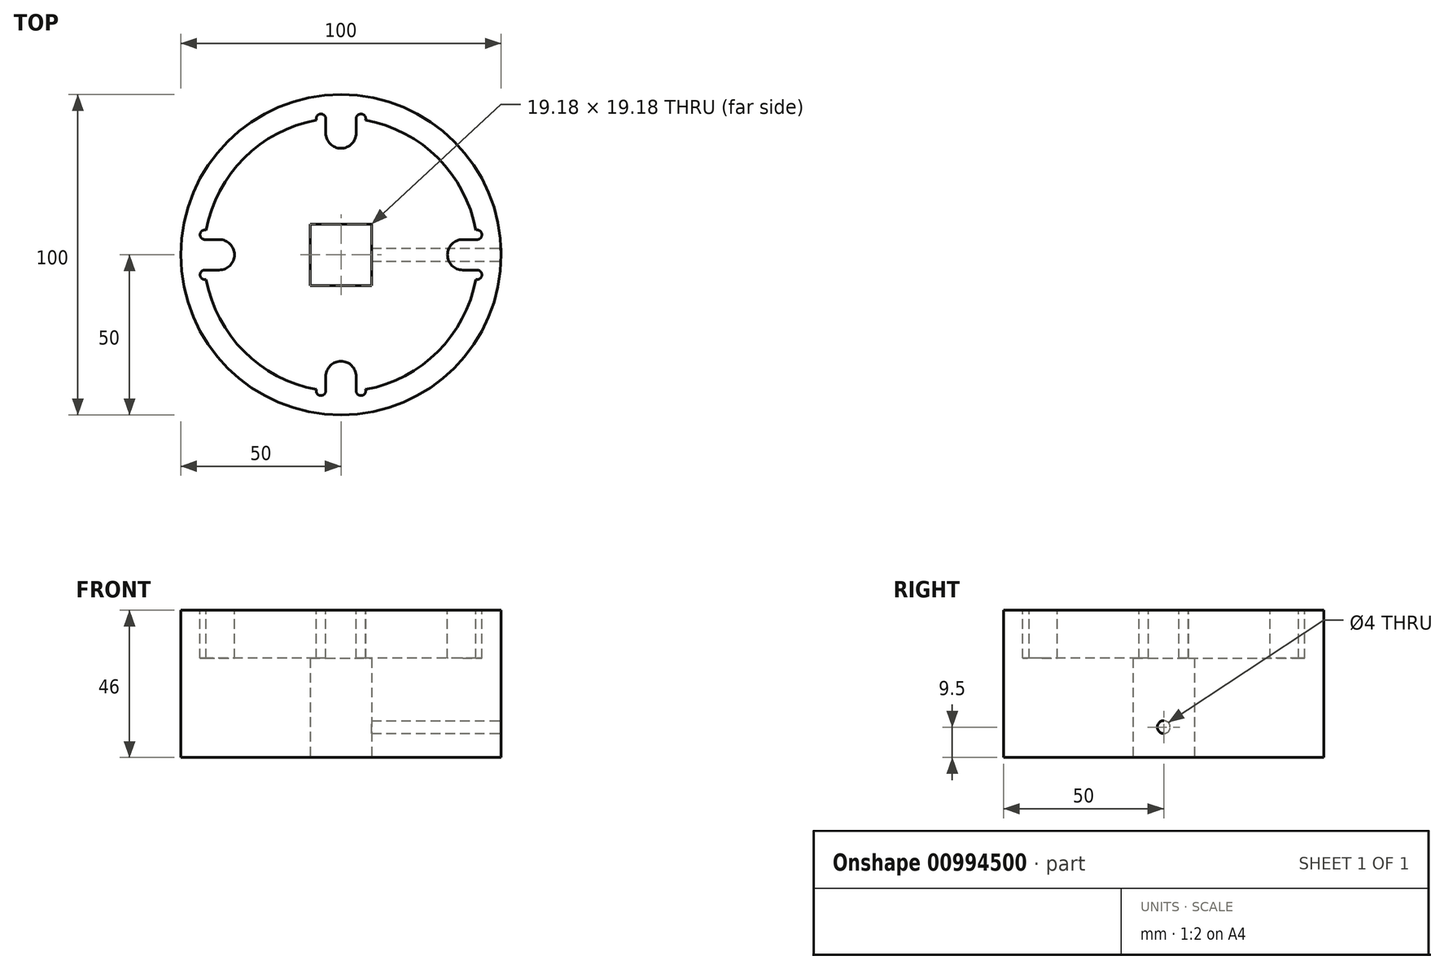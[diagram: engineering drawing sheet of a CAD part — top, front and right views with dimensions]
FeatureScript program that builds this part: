
annotation { "Feature Type Name" : "Feature", "Feature Type Description" : "" }
export const myFeature = defineFeature(function(context is Context, id is Id, definition is map)
    precondition{}
    {
        {
            var Q0;
            Q0=qCreatedBy(makeId("Top.planeOp"),FACE);
            var sketch = newSketch(context, id + "F0", { "sketchPlane" : qUnion([Q0])});
            skCircle(sketch, "E0", {"center": v(0, 0) * mm, "radius": 50 * mm});
            skSolve(sketch);
        }
        {
            var Q0;
            Q0 = qSketchRegion(id + "F0", true);
            extrude(context, id + "F1", {"entities" : qUnion([Q0]), "depth" : 46 * mm, "offsetDistance" : 25 * mm});
        }
        {
            var Q0;
            Q0=makeQuery(id+"F1.opExtrude","CAP_FACE",FACE,{"disambiguationData":[OSD([sQuery(id+"F0.wireOp",EDGE,"E0")])],"isStart":false});
            var sketch = newSketch(context, id + "F2", { "sketchPlane" : qUnion([Q0])});
            skArc(sketch, "E1", {"start": v(-7.69, 42.05) * mm, "mid": v(-30.23, 30.23) * mm, "end": v(-42.05, 7.69) * mm});
            skLineSegment(sketch, "E2.0", {"start": v(-42.49, -4.75) * mm, "end": v(-38, -4.75) * mm});
            skLineSegment(sketch, "E3.0", {"start": v(-42.49, 4.75) * mm, "end": v(-38, 4.75) * mm});
            skLineSegment(sketch, "E4.0", {"start": v(-4.75, 42.49) * mm, "end": v(-4.75, 38) * mm});
            skLineSegment(sketch, "E5.0", {"start": v(4.75, 42.49) * mm, "end": v(4.75, 38) * mm});
            skArc(sketch, "E6.trimOffspring", {"start": v(-42.05, -7.69) * mm, "mid": v(-30.23, -30.23) * mm, "end": v(-7.69, -42.05) * mm});
            skArc(sketch, "E7.trimOffspring", {"start": v(7.69, -42.05) * mm, "mid": v(30.23, -30.23) * mm, "end": v(42.05, -7.69) * mm});
            skLineSegment(sketch, "E8.trimOffspring", {"start": v(38, 4.75) * mm, "end": v(42.49, 4.75) * mm});
            skLineSegment(sketch, "E9.trimOffspring", {"start": v(38, -4.75) * mm, "end": v(42.49, -4.75) * mm});
            skLineSegment(sketch, "E10.trimOffspring", {"start": v(-4.75, -38) * mm, "end": v(-4.75, -42.49) * mm});
            skLineSegment(sketch, "E11.trimOffspring", {"start": v(4.75, -38) * mm, "end": v(4.75, -42.49) * mm});
            skArc(sketch, "E12.trimOffspring", {"start": v(42.05, 7.69) * mm, "mid": v(30.23, 30.23) * mm, "end": v(7.69, 42.05) * mm});
            skArc(sketch, "E13", {"start": v(-38, -4.75) * mm, "mid": v(-33.25, 0) * mm, "end": v(-38, 4.75) * mm});
            skArc(sketch, "E14", {"start": v(4.75, -38) * mm, "mid": v(0, -33.25) * mm, "end": v(-4.75, -38) * mm});
            skArc(sketch, "E15", {"start": v(-4.75, 38) * mm, "mid": v(0, 33.25) * mm, "end": v(4.75, 38) * mm});
            skArc(sketch, "E16", {"start": v(38, 4.75) * mm, "mid": v(33.25, 0) * mm, "end": v(38, -4.75) * mm});
            skArc(sketch, "E17", {"start": v(7.69, 42.05) * mm, "mid": v(6.47, 43.97) * mm, "end": v(4.75, 42.49) * mm});
            skArc(sketch, "E18", {"start": v(-4.75, 42.49) * mm, "mid": v(-6.47, 43.97) * mm, "end": v(-7.69, 42.05) * mm});
            skArc(sketch, "E19", {"start": v(42.49, 4.75) * mm, "mid": v(43.97, 6.47) * mm, "end": v(42.05, 7.69) * mm});
            skArc(sketch, "E20", {"start": v(42.05, -7.69) * mm, "mid": v(43.97, -6.47) * mm, "end": v(42.49, -4.75) * mm});
            skArc(sketch, "E21", {"start": v(-42.05, 7.69) * mm, "mid": v(-43.97, 6.47) * mm, "end": v(-42.49, 4.75) * mm});
            skArc(sketch, "E22", {"start": v(-42.49, -4.75) * mm, "mid": v(-43.97, -6.47) * mm, "end": v(-42.05, -7.69) * mm});
            skArc(sketch, "E23", {"start": v(4.75, -42.49) * mm, "mid": v(6.47, -43.97) * mm, "end": v(7.69, -42.05) * mm});
            skArc(sketch, "E24", {"start": v(-7.69, -42.05) * mm, "mid": v(-6.47, -43.97) * mm, "end": v(-4.75, -42.49) * mm});
            skSolve(sketch);
        }
        {
            var Q0;
            Q0 = qSketchRegion(id + "F2", true);
            extrude(context, id + "F3", {"entities" : qUnion([Q0]), "operationType" : NewBodyOperationType.REMOVE, "oppositeDirection" : true, "depth" : 15 * mm, "offsetDistance" : 25 * mm});
        }
        {
            var Q0;
            Q0=makeQuery(id+"F1.opExtrude","CAP_FACE",FACE,{"disambiguationData":[OSD([sQuery(id+"F0.wireOp",EDGE,"E0")])],"isStart":true});
            var sketch = newSketch(context, id + "F4", { "sketchPlane" : qUnion([Q0])});
            skLineSegment(sketch, "E25.bottom", {"start": v(9.59, -9.59) * mm, "end": v(-9.59, -9.59) * mm});
            skLineSegment(sketch, "E25.top", {"start": v(9.59, 9.59) * mm, "end": v(-9.59, 9.59) * mm});
            skLineSegment(sketch, "E25.left", {"start": v(9.59, -9.59) * mm, "end": v(9.59, 9.59) * mm});
            skLineSegment(sketch, "E25.right", {"start": v(-9.59, -9.59) * mm, "end": v(-9.59, 9.59) * mm});
            skPoint(sketch, "E25.middle", {"position": v(0, 0) * mm});
            skSolve(sketch);
        }
        {
            var Q0;
            Q0 = qSketchRegion(id + "F4", true);
            extrude(context, id + "F5", {"entities" : qUnion([Q0]), "operationType" : NewBodyOperationType.REMOVE, "endBound" : BoundingType.THROUGH_ALL, "oppositeDirection" : true, "depth" : 23 * mm, "offsetDistance" : 25 * mm});
        }
        {
            var Q0;
            Q0=qCreatedBy(makeId("Right.planeOp"),FACE);
            cPlane(context, id + "F6", {"entities" : qUnion([Q0]), "cplaneType" : CPlaneType.OFFSET, "offset" : 50 * mm, "width" : 150 * mm, "height" : 150 * mm});
        }
        {
            var Q0;
            Q0=qCreatedBy(id+"F6.planeOp",FACE);
            var sketch = newSketch(context, id + "F7", { "sketchPlane" : qUnion([Q0])});
            skCircle(sketch, "E26", {"center": v(0, 9.5) * mm, "radius": 2 * mm});
            skSolve(sketch);
        }
        {
            var Q0;
            Q0 = qSketchRegion(id + "F7", true);
            extrude(context, id + "F8", {"entities" : qUnion([Q0]), "operationType" : NewBodyOperationType.REMOVE, "endBound" : BoundingType.UP_TO_NEXT, "oppositeDirection" : true, "depth" : 25 * mm, "offsetDistance" : 25 * mm});
        }
    });
